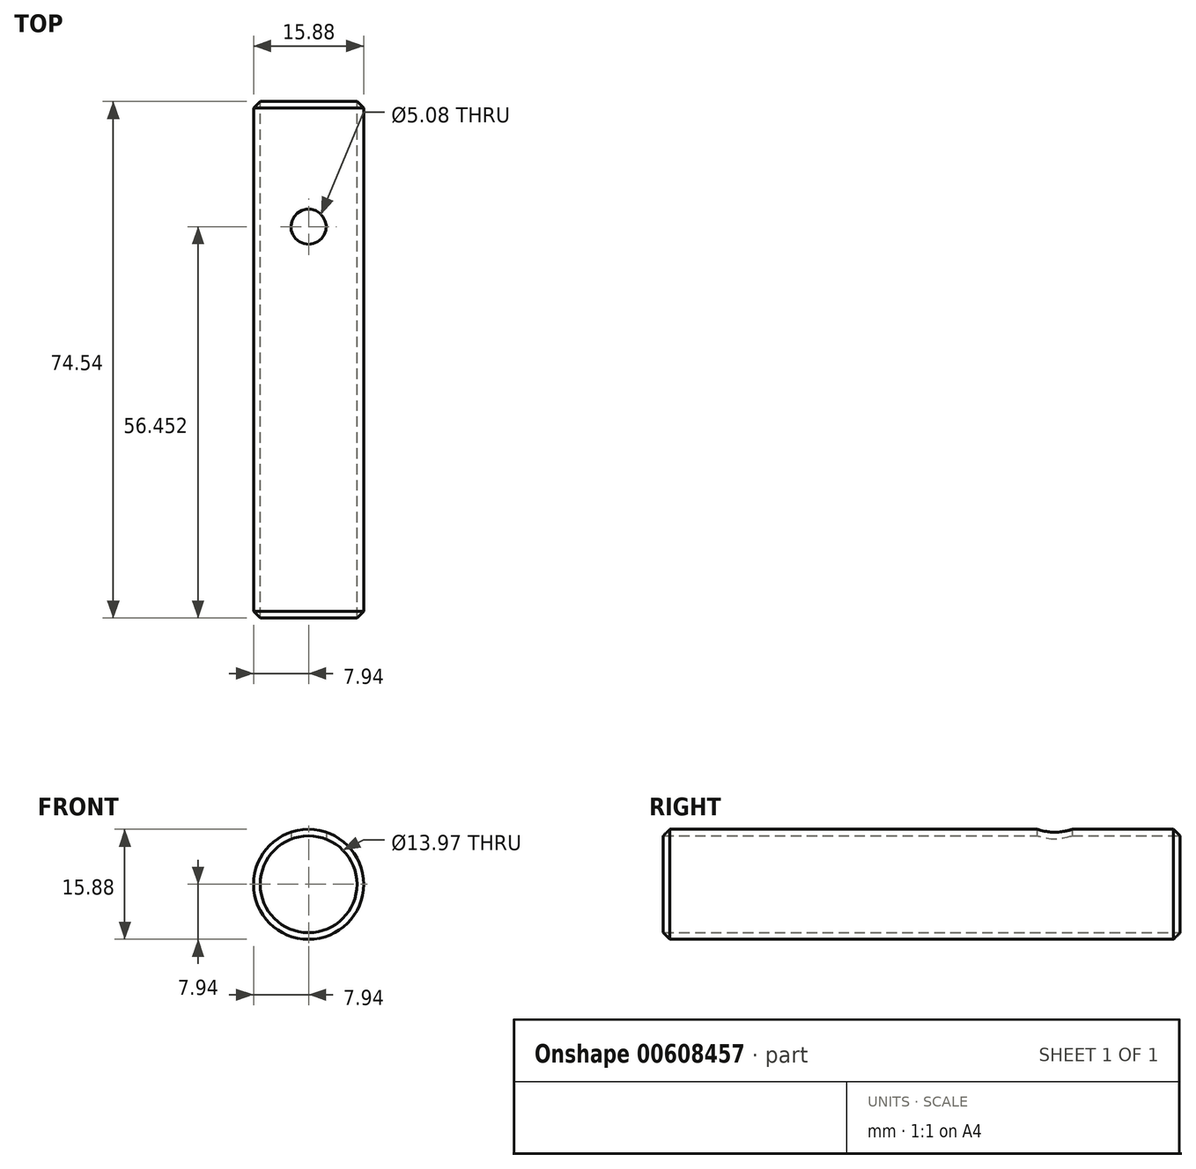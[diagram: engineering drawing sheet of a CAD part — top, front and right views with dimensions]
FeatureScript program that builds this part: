
annotation { "Feature Type Name" : "Feature", "Feature Type Description" : "" }
export const myFeature = defineFeature(function(context is Context, id is Id, definition is map)
    precondition{}
    {
        {
            var Q0;
            Q0=qCreatedBy(makeId("Front.planeOp"),FACE);
            var sketch = newSketch(context, id + "F0", { "sketchPlane" : qUnion([Q0])});
            skCircle(sketch, "E0", {"center": v(0, 0) * mm, "radius": 7.94 * mm});
            skSolve(sketch);
        }
        {
            var Q0;
            Q0=makeQuery(id+"F0.imprint","IMPRINT",FACE,{"disambiguationData":[TD([[makeQuery(id+"F0.imprint","IMPRINT",EDGE,{"derivedFrom":sQuery(id+"F0.wireOp",EDGE,"E0")}),1.0]])]});
            extrude(context, id + "F1", {"entities" : qUnion([Q0]), "depth" : 76.2 * mm, "offsetDistance" : 25.4 * mm});
        }
        {
            var Q0;
            Q0=qCreatedBy(makeId("Front.planeOp"),FACE);
            var sketch = newSketch(context, id + "F2", { "sketchPlane" : qUnion([Q0])});
            skPoint(sketch, "E1", {"position": v(0, 0) * mm});
            skSolve(sketch);
        }
        {
            var Q0;
            Q0=sQuery(id+"F2.wireOp",VERTEX,"E1");
            var Q1;
            Q1=makeQuery(id+"F1.opExtrude","SWEPT_BODY",BODY,{"disambiguationData":[OSD([sQuery(id+"F0.wireOp",EDGE,"E0")])]});
            hole(context, id + "F3", {"style" : HoleStyle.SIMPLE, "endStyle" : HoleEndStyle.BLIND, "oppositeDirection" : true, "holeDiameter" : 13.97 * mm, "majorDiameter" : 6.35 * mm, "holeDepth" : 76.2 * mm, "isTappedThrough" : true, "tappedDepth" : 12.7 * mm, "tapClearance" : 3, "startFromSketch" : true, "locations" : qUnion([Q0]), "scope" : qUnion([Q1])});
        }
        {
            var Q0;
            Q0=makeQuery(id+"F1.opExtrude","CAP_EDGE",EDGE,{"disambiguationData":[OSD([sQuery(id+"F0.wireOp",EDGE,"E0")])],"isStart":false});
            chamfer(context, id + "F4", {"entities" : qUnion([Q0]), "width" : 1.78 * mm, "tangentPropagation" : true});
        }
        {
            var Q0;
            Q0=makeQuery(id+"F1.opExtrude","CAP_EDGE",EDGE,{"disambiguationData":[OSD([sQuery(id+"F0.wireOp",EDGE,"E0")])],"isStart":true});
            chamfer(context, id + "F5", {"entities" : qUnion([Q0]), "width" : 1.78 * mm, "tangentPropagation" : true});
        }
        {
            var Q0;
            Q0=qCreatedBy(makeId("Top.planeOp"),FACE);
            var sketch = newSketch(context, id + "F6", { "sketchPlane" : qUnion([Q0])});
            skPoint(sketch, "E2", {"position": v(0, -18.92) * mm});
            skSolve(sketch);
        }
        {
            var Q0;
            Q0=sQuery(id+"F6.wireOp",VERTEX,"E2");
            var Q1;
            Q1=makeQuery(id+"F1.opExtrude","SWEPT_BODY",BODY,{"disambiguationData":[OSD([sQuery(id+"F0.wireOp",EDGE,"E0")])]});
            hole(context, id + "F7", {"style" : HoleStyle.SIMPLE, "endStyle" : HoleEndStyle.BLIND, "oppositeDirection" : true, "holeDiameter" : 5.08 * mm, "majorDiameter" : 6.35 * mm, "holeDepth" : 25.4 * mm, "isTappedThrough" : true, "tappedDepth" : 12.7 * mm, "tapClearance" : 3, "startFromSketch" : true, "locations" : qUnion([Q0]), "scope" : qUnion([Q1])});
        }
    });
